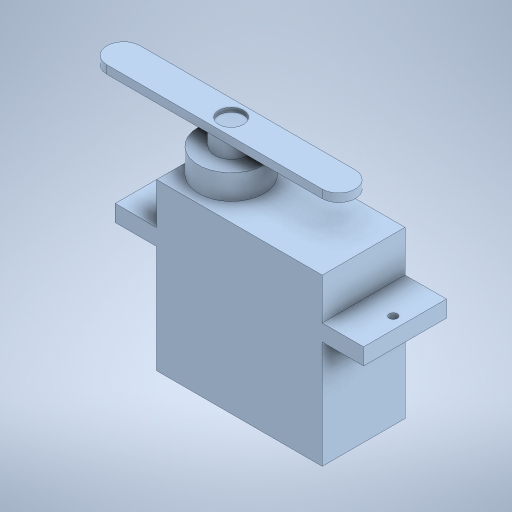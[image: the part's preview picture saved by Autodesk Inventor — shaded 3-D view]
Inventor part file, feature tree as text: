
AUTODESK INVENTOR PART (.ipt)
format: ipt  version: 2023 (Build 270158000, 158)  size: 299,008 bytes
history: native  units: in
note: dims shown in document units (in); Inventor stores cm internally (conversion verified against a paired STEP export)
features: extrude x8, sketch x8
ambient origin geometry x8: Origin, YZ Plane, XZ Plane, XY Plane, X Axis, Y Axis, Z Axis, Center Point
bodies: Solid1 (feature_tree)
feature tree (16):
  extrude  "Extrusion1"  Depth=0.7874in
  extrude  "Extrusion2"  Depth=0.3937in
  extrude  "Extrusion3"  Depth=0.1969in TaperAngle=0.0deg
  extrude  "Extrusion4"  Depth=0.1969in TaperAngle=0.0deg
  extrude  "Extrusion5"  TaperAngle=0.0deg  [1 undecoded]
  extrude  "Extrusion6"  Depth=0.1575in
  extrude  "Extrusion7"  Depth=0.5906in
  extrude  "Extrusion8"  Depth=0.0787in
  sketch  "Sketch1"  dims[d0=0.7874in d1=0.7874in]
  sketch  "Sketch2"  dims[d2=0.3937in d3=0.0in d4=0.3937in]
  sketch  "Sketch3"  dims[d5=0.0787in d6=0.1969in d7=0.0in]
  sketch  "Sketch4"  dims[d8=0.0787in d9=0.1969in d10=0.0in]
  sketch  "Sketch5"  dims[d11=0.0394in d12=0.0in d13=0.0in]
  sketch  "Sketch6"  dims[d14=0.1181in d15=0.0in d16=0.1575in]
  sketch  "Sketch7"  dims[d17=0.0787in d18=0.0in d19=0.5906in]
  sketch  "Sketch8"  dims[d20=0.5906in d21=0.0787in d22=0.0394in d23=0.0in d24=0.1181in d25=0.0197in d26=0.0in]
note: 1 required parameter value undecoded (feature->parameter linkage not recoverable at this tier; creation-order binding heuristic only, values carry confidence <= 0.55)
